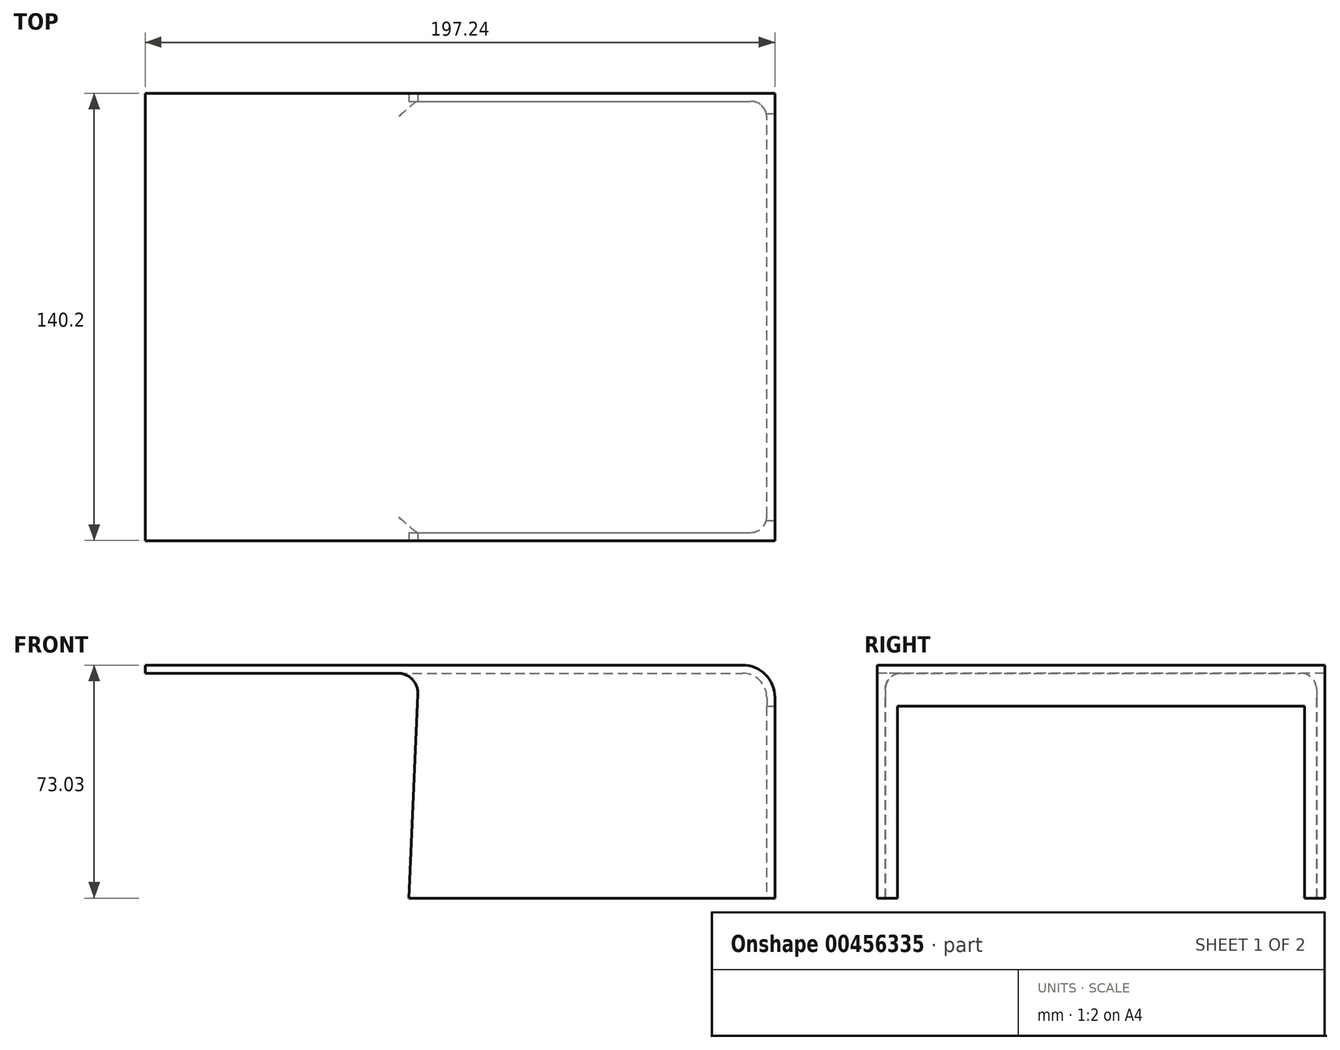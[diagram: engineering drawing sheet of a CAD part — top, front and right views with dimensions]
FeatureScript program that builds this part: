
annotation { "Feature Type Name" : "Feature", "Feature Type Description" : "" }
export const myFeature = defineFeature(function(context is Context, id is Id, definition is map)
    precondition{}
    {
        {
            var Q0;
            Q0=qCreatedBy(makeId("Top.planeOp"),FACE);
            var sketch = newSketch(context, id + "F0", { "sketchPlane" : qUnion([Q0])});
            skLineSegment(sketch, "E0.bottom", {"start": v(-98.62, 70.1) * mm, "end": v(98.62, 70.1) * mm});
            skLineSegment(sketch, "E0.top", {"start": v(-98.62, -70.1) * mm, "end": v(98.62, -70.1) * mm});
            skLineSegment(sketch, "E0.left", {"start": v(-98.62, 70.1) * mm, "end": v(-98.62, -70.1) * mm});
            skLineSegment(sketch, "E0.right", {"start": v(98.62, 70.1) * mm, "end": v(98.62, -70.1) * mm});
            skPoint(sketch, "E0.middle", {"position": v(0, 0) * mm});
            skSolve(sketch);
        }
        {
            var Q0;
            Q0=makeQuery(id+"F0.imprint","IMPRINT",FACE,{"disambiguationData":[TD([[makeQuery(id+"F0.imprint","IMPRINT",EDGE,{"derivedFrom":sQuery(id+"F0.wireOp",EDGE,"E0.bottom")}),-1.0]])]});
            extrude(context, id + "F1", {"entities" : qUnion([Q0]), "depth" : 73.02 * mm});
        }
        {
            var Q0;
            Q0=makeQuery(id+"F1.opExtrude","CAP_EDGE",EDGE,{"disambiguationData":[OSD([sQuery(id+"F0.wireOp",EDGE,"E0.right")])],"isStart":false});
            fillet(context, id + "F2", {"entities" : qUnion([Q0]), "radius" : 10.16 * mm, "tangentPropagation" : true, "allowEdgeOverflow" : false});
        }
        {
            var Q0;
            Q0=makeQuery(id+"F1.opExtrude","CAP_FACE",FACE,{"disambiguationData":[OSD([sQuery(id+"F0.wireOp",EDGE,"E0.bottom"),sQuery(id+"F0.wireOp",EDGE,"E0.top"),sQuery(id+"F0.wireOp",EDGE,"E0.left"),sQuery(id+"F0.wireOp",EDGE,"E0.right")])],"isStart":true});
            shell(context, id + "F3", {"entities" : qUnion([Q0]), "thickness" : 2.54 * mm});
        }
        {
            var Q0;
            Q0=makeQuery(id+"F1.opExtrude","SWEPT_FACE",FACE,{"disambiguationData":[OSD([sQuery(id+"F0.wireOp",EDGE,"E0.left")])]});
            var sketch = newSketch(context, id + "F4", { "sketchPlane" : qUnion([Q0])});
            skLineSegment(sketch, "E1.bottom", {"start": v(-81.13, 0) * mm, "end": v(67.56, 0) * mm});
            skLineSegment(sketch, "E1.top", {"start": v(-81.13, 70.48) * mm, "end": v(67.56, 70.49) * mm});
            skLineSegment(sketch, "E1.left", {"start": v(-81.13, 0) * mm, "end": v(-81.13, 70.48) * mm});
            skLineSegment(sketch, "E1.right", {"start": v(67.56, 0) * mm, "end": v(67.56, 70.49) * mm});
            skSolve(sketch);
        }
        {
            var Q0;
            Q0=makeQuery(id+"F4.imprint","IMPRINT",FACE,{"disambiguationData":[TD([[makeQuery(id+"F4.imprint","IMPRINT",EDGE,{"derivedFrom":sQuery(id+"F4.wireOp",EDGE,"E1.bottom")}),1.0]])]});
            extrude(context, id + "F5", {"entities" : qUnion([Q0]), "operationType" : NewBodyOperationType.REMOVE, "oppositeDirection" : true, "depth" : 25.4 * mm});
        }
        {
            var Q0;
            {var subQ0=sQuery(id+"F0.wireOp",EDGE,"E0.top");var subQ1=sQuery(id+"F0.wireOp",EDGE,"E0.right");Q0=makeQuery(id+"F3.opShell","OFFSET_EDGE",EDGE,{"disambiguationData":[OSD([subQ0,subQ1]),TDD([makeQuery(id+"F2.opFillet","BLEND_EDGE",EDGE,{"blendedFrom":[makeQuery(id+"F1.opExtrude","CAP_EDGE",EDGE,{"disambiguationData":[OSD([subQ1])],"isStart":false}),makeQuery(id+"F1.opExtrude","SWEPT_FACE",FACE,{"disambiguationData":[OSD([subQ0])]})],"blendedInto":[makeQuery(id+"F1.opExtrude","SWEPT_FACE",FACE,{"disambiguationData":[OSD([subQ0])]})]})])]});}
            var Q1;
            {var subQ0=sQuery(id+"F0.wireOp",EDGE,"E0.bottom");var subQ1=sQuery(id+"F0.wireOp",EDGE,"E0.right");Q1=makeQuery(id+"F3.opShell","OFFSET_EDGE",EDGE,{"disambiguationData":[OSD([subQ0,subQ1]),TDD([makeQuery(id+"F2.opFillet","BLEND_EDGE",EDGE,{"blendedFrom":[makeQuery(id+"F1.opExtrude","CAP_EDGE",EDGE,{"disambiguationData":[OSD([subQ1])],"isStart":false}),makeQuery(id+"F1.opExtrude","SWEPT_FACE",FACE,{"disambiguationData":[OSD([subQ0])]})],"blendedInto":[makeQuery(id+"F1.opExtrude","SWEPT_FACE",FACE,{"disambiguationData":[OSD([subQ0])]})]})])]});}
            fillet(context, id + "F6", {"entities" : qUnion([Q0, Q1]), "radius" : 5.08 * mm, "tangentPropagation" : true, "allowEdgeOverflow" : false});
        }
        {
            var Q0;
            Q0=makeQuery(id+"F1.opExtrude","SWEPT_FACE",FACE,{"disambiguationData":[OSD([sQuery(id+"F0.wireOp",EDGE,"E0.right")])]});
            var sketch = newSketch(context, id + "F7", { "sketchPlane" : qUnion([Q0])});
            skLineSegment(sketch, "E2.bottom", {"start": v(-63.75, 0) * mm, "end": v(63.75, 0) * mm});
            skLineSegment(sketch, "E2.top", {"start": v(-63.75, 60.12) * mm, "end": v(63.75, 60.12) * mm});
            skLineSegment(sketch, "E2.left", {"start": v(-63.75, 0) * mm, "end": v(-63.75, 60.12) * mm});
            skLineSegment(sketch, "E2.right", {"start": v(63.75, 0) * mm, "end": v(63.75, 60.12) * mm});
            skSolve(sketch);
        }
        {
            var Q0;
            Q0=makeQuery(id+"F7.imprint","IMPRINT",FACE,{"disambiguationData":[TD([[makeQuery(id+"F7.imprint","IMPRINT",EDGE,{"derivedFrom":sQuery(id+"F7.wireOp",EDGE,"E2.bottom")}),-1.0]])]});
            extrude(context, id + "F8", {"entities" : qUnion([Q0]), "operationType" : NewBodyOperationType.REMOVE, "oppositeDirection" : true, "depth" : 25.4 * mm});
        }
        {
            var Q0;
            Q0=makeQuery(id+"F1.opExtrude","SWEPT_FACE",FACE,{"disambiguationData":[OSD([sQuery(id+"F0.wireOp",EDGE,"E0.top")])]});
            var sketch = newSketch(context, id + "F9", { "sketchPlane" : qUnion([Q0])});
            skLineSegment(sketch, "E3.bottom", {"start": v(-98.62, 0) * mm, "end": v(-16.07, 0) * mm});
            skLineSegment(sketch, "E3.top", {"start": v(-98.62, 70.48) * mm, "end": v(-19.53, 70.48) * mm});
            skLineSegment(sketch, "E3.left", {"start": v(-98.62, 0) * mm, "end": v(-98.62, 70.48) * mm});
            skLineSegment(sketch, "E4", {"start": v(-13.19, 63.85) * mm, "end": v(-16.07, 0) * mm});
            skPoint(sketch, "E5.visualSharp", {"position": v(-12.9, 70.48) * mm});
            skArc(sketch, "E5.filletArc", {"start": v(-13.19, 63.85) * mm, "mid": v(-14.94, 68.52) * mm, "end": v(-19.53, 70.48) * mm});
            skSolve(sketch);
        }
        {
            var Q0;
            Q0 = qSketchRegion(id + "F9", true);
            extrude(context, id + "F10", {"entities" : qUnion([Q0]), "operationType" : NewBodyOperationType.REMOVE, "oppositeDirection" : true, "depth" : 254 * mm});
        }
    });
